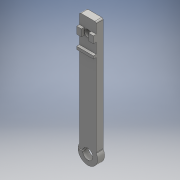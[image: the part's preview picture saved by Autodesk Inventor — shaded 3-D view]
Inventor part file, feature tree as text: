
AUTODESK INVENTOR PART (.ipt)
format: ipt  version: 2016 (Build 200138000, 138)  size: 209,920 bytes
history: native  units: mm
features: sketch x7, extrude x6, projected_geometry x5, fillet x2, hole x1, draft x1
ambient origin geometry x8: Origin, YZ Plane, XZ Plane, XY Plane, X Axis, Y Axis, Z Axis, Center Point
bodies: Solid1 (feature_tree)
feature tree (22):
  extrude  "Extrusion1"  Depth=10.0mm
  hole  "Hole1"  [1 undecoded]
  draft  "FaceDraft1"
  extrude  "Extrusion2"  Depth=10.0mm TaperAngle=0.0deg
  fillet  "Fillet2"  Radius=0.5mm
  extrude  "Extrusion3"  Depth=10.0mm
  extrude  "Extrusion4"  Depth=5.0mm
  extrude  "Extrusion5"  Depth=5.1mm
  extrude  "Extrusion6"  Depth=1.0mm TaperAngle=0.0deg
  fillet  "Fillet4"  Radius=1.0mm
  sketch  "Sketch1"  dims[d3=5.0mm d4=0.0mm d5=10.0mm]
  sketch  "Sketch2"  dims[d6=5.1mm d7=6.0mm d8=4.0mm d9=2.0mm d10=90.0deg d11=8.0mm d12=20.594885mm d14=15.0deg]
  sketch  "Sketch3"  dims[d15=0.6mm d16=10.0mm d17=0.0mm d18=0.5mm]
  sketch  "Sketch4"  dims[d19=10.0mm d21=20.0mm]
  sketch  "Sketch5"  dims[d22=2.0mm d23=5.0mm]
  projected_geometry  "Projected Loop1"
  sketch  "Sketch6"  dims[d24=2.0mm d25=0.0mm d26=5.1mm]
  projected_geometry  "Projected Loop2"
  projected_geometry  "Projected Loop3"
  sketch  "Sketch7"  dims[d27=5.1mm d28=2.0mm d29=0.0mm d32=1.0mm d33=0.0mm d34=1.0mm d35=0.0mm d36=1.0mm]
  projected_geometry  "Projected Loop4"
  projected_geometry  "Projected Loop5"
note: 1 required parameter value undecoded (feature->parameter linkage not recoverable at this tier; creation-order binding heuristic only, values carry confidence <= 0.55)
